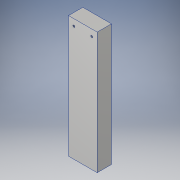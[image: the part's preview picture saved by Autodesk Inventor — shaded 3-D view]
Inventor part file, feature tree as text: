
AUTODESK INVENTOR PART (.ipt)
format: ipt  version: 2019 (Build 230136000, 136)  size: 105,984 bytes
history: native  units: in
note: dims shown in document units (in); Inventor stores cm internally (conversion verified against a paired STEP export)
features: sketch x2, extrude x1, hole x1
ambient origin geometry x8: Origin, YZ Plane, XZ Plane, XY Plane, X Axis, Y Axis, Z Axis, Center Point
bodies: Solid1 (feature_tree)
feature tree (4):
  extrude  "Extrusion1"  Depth=4.25in
  hole  "Hole1"  [1 undecoded]
  sketch  "Sketch1"  dims[d0=1.0in d1=4.25in]
  sketch  "Sketch2"  dims[d2=0.5in d3=0.0in d4=0.625in d5=0.228in d6=0.228in d7=1.0in d8=0.1875in d9=0.067in d10=0.172in d11=0.375in d12=0.25in d13=0.5635in d14=0.261in d15=0.8108in]
note: 1 required parameter value undecoded (feature->parameter linkage not recoverable at this tier; creation-order binding heuristic only, values carry confidence <= 0.55)
